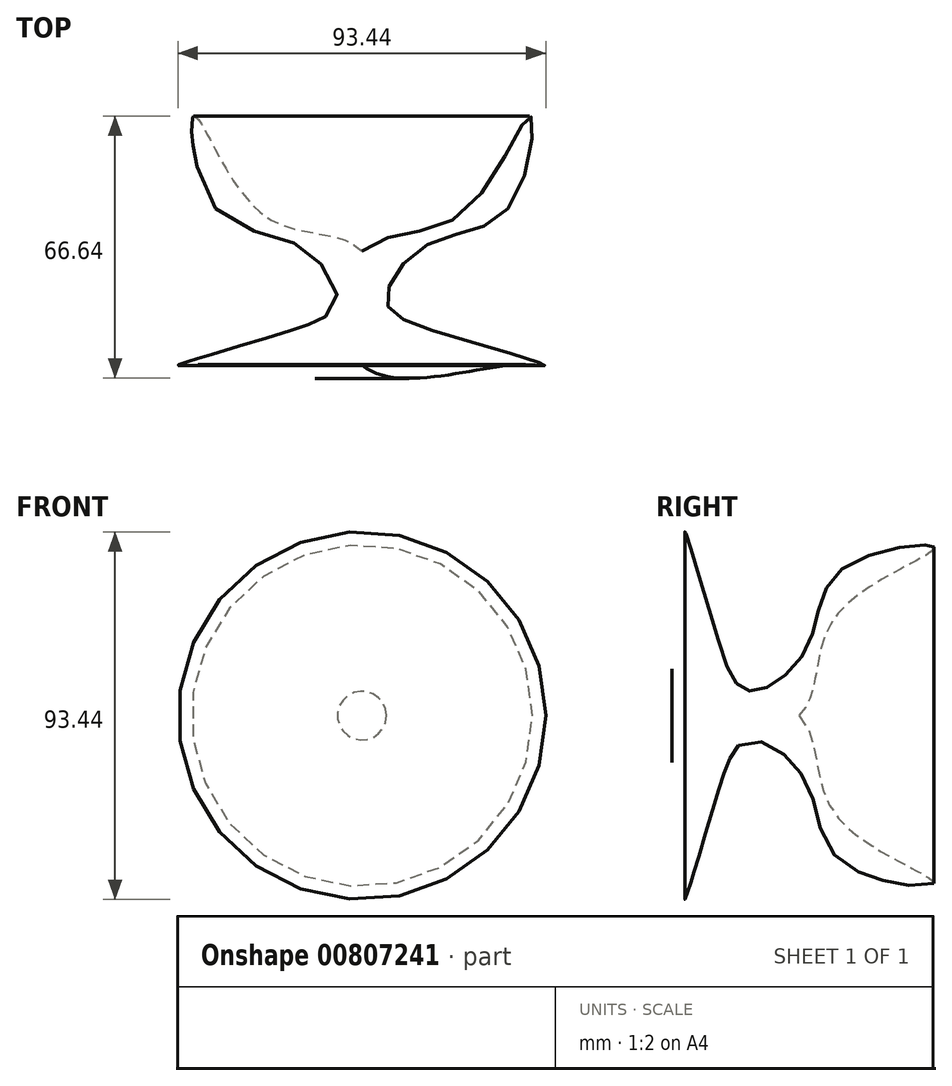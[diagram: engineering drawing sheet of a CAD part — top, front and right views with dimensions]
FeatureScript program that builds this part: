
annotation { "Feature Type Name" : "Feature", "Feature Type Description" : "" }
export const myFeature = defineFeature(function(context is Context, id is Id, definition is map)
    precondition{}
    {
        {
            var Q0;
            Q0=qCreatedBy(makeId("Top.planeOp"),FACE);
            var sketch = newSketch(context, id + "F0", { "sketchPlane" : qUnion([Q0])});
            skLineSegment(sketch, "E0", {"start": v(0, 98.18) * mm, "end": v(0, -93.81) * mm});
            skFitSpline(sketch, "E1", {"points": [v(42.7, 63.25) * mm, v(37.46, 40.12) * mm, v(16.86, 30.75) * mm, v(6.24, 16.39) * mm, v(19.67, 8.27) * mm, v(46.66, 0) * mm, v(38.31, 0) * mm, v(0, 0) * mm, v(0, 28.88) * mm, v(25.6, 38.56) * mm, v(42.7, 63.25) * mm]});
            skSolve(sketch);
        }
        {
            var Q0;
            {var subQ0=sQuery(id+"F0.wireOp",EDGE,"E1");var subQ1=sQuery(id+"F0.wireOp",EDGE,"E0");var subQ2=makeQuery(id+"F0.imprint","INTERSECT",VERTEX,{"disambiguationData":[OD(0.0)],"derivedFrom":[subQ1,subQ0]});Q0=makeQuery(id+"F0.imprint","IMPRINT",FACE,{"disambiguationData":[TD([[makeQuery(id+"F0.imprint","IMPRINT",EDGE,{"disambiguationData":[TD([[subQ2,1.0]])],"derivedFrom":subQ1}),1.0]])]});}
            var Q1;
            Q1=sQuery(id+"F0.wireOp",EDGE,"E0");
            revolve(context, id + "F1", {"surfaceOperationType" : NewSurfaceOperationType.NEW, "entities" : qUnion([Q0]), "axis" : qUnion([Q1]), "revolveType" : RevolveType.FULL});
        }
        {
            var Q0;
            Q0=qCreatedBy(makeId("Right.planeOp"),FACE);
            var sketch = newSketch(context, id + "F2", { "sketchPlane" : qUnion([Q0])});
            skFitSpline(sketch, "E2", {"points": [v(53.17, 39.11) * mm, v(46.62, 57.83) * mm, v(40.07, 30.22) * mm], "startDerivative": vector(-14.92, 62) * mm, "endDerivative": vector(-11.39, -75.69) * mm});
            skSolve(sketch);
        }
        {
            var Q0;
            Q0=sQuery(id+"F2.wireOp",VERTEX,"E2.end");
            var Q1;
            Q1=sQuery(id+"F2.wireOp",EDGE,"E2");
            cPlane(context, id + "F3", {"entities" : qUnion([Q0, Q1]), "cplaneType" : CPlaneType.CURVE_POINT, "offset" : 25.4 * mm, "width" : 152.4 * mm, "height" : 152.4 * mm});
        }
    });
